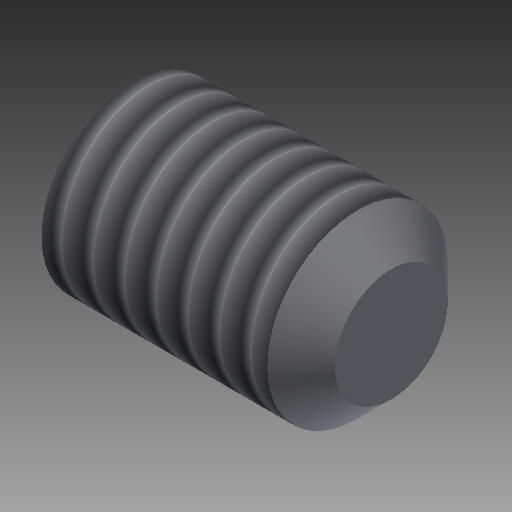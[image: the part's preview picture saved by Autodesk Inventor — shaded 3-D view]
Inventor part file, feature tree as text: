
AUTODESK INVENTOR PART (.ipt)
format: ipt  version: 2019 (Build 230136000, 136)  size: 216,576 bytes
history: native  units: mm
features: other x14, sketch x2, revolve x1, thread x1, extrude x1
ambient origin geometry x8: Origin, YZ Plane, XZ Plane, XY Plane, X Axis, Y Axis, Z Axis, Center Point
bodies: Solid1 (feature_tree)
feature tree (19):
  revolve  "Revolution1"  [1 undecoded]
  thread  "Thread1"  [1 undecoded]
  extrude  "Extrusion1"  [1 undecoded]
  other  "IP1_XY"
  other  "IP1_YZ"
  other  "IP1_ZX"
  other  "IP1_X"
  other  "IP1_Y"
  other  "IP1_Z"
  other  "IP1_Center"
  other  "IP2_XY"
  other  "IP2_YZ"
  other  "IP2_ZX"
  other  "IP2_X"
  other  "IP2_Y"
  other  "IP2_Z"
  other  "IP2_Center"
  sketch  "Sketch_1"  dims[d0=360.0deg d1=5.00203mm d2=0.0mm d3=2.5mm d4=0.0mm]
  sketch  "Sketch_2"  dims[d5=0.0mm d6=0.0mm]
note: 3 required parameter values undecoded (feature->parameter linkage not recoverable at this tier; creation-order binding heuristic only, values carry confidence <= 0.55)